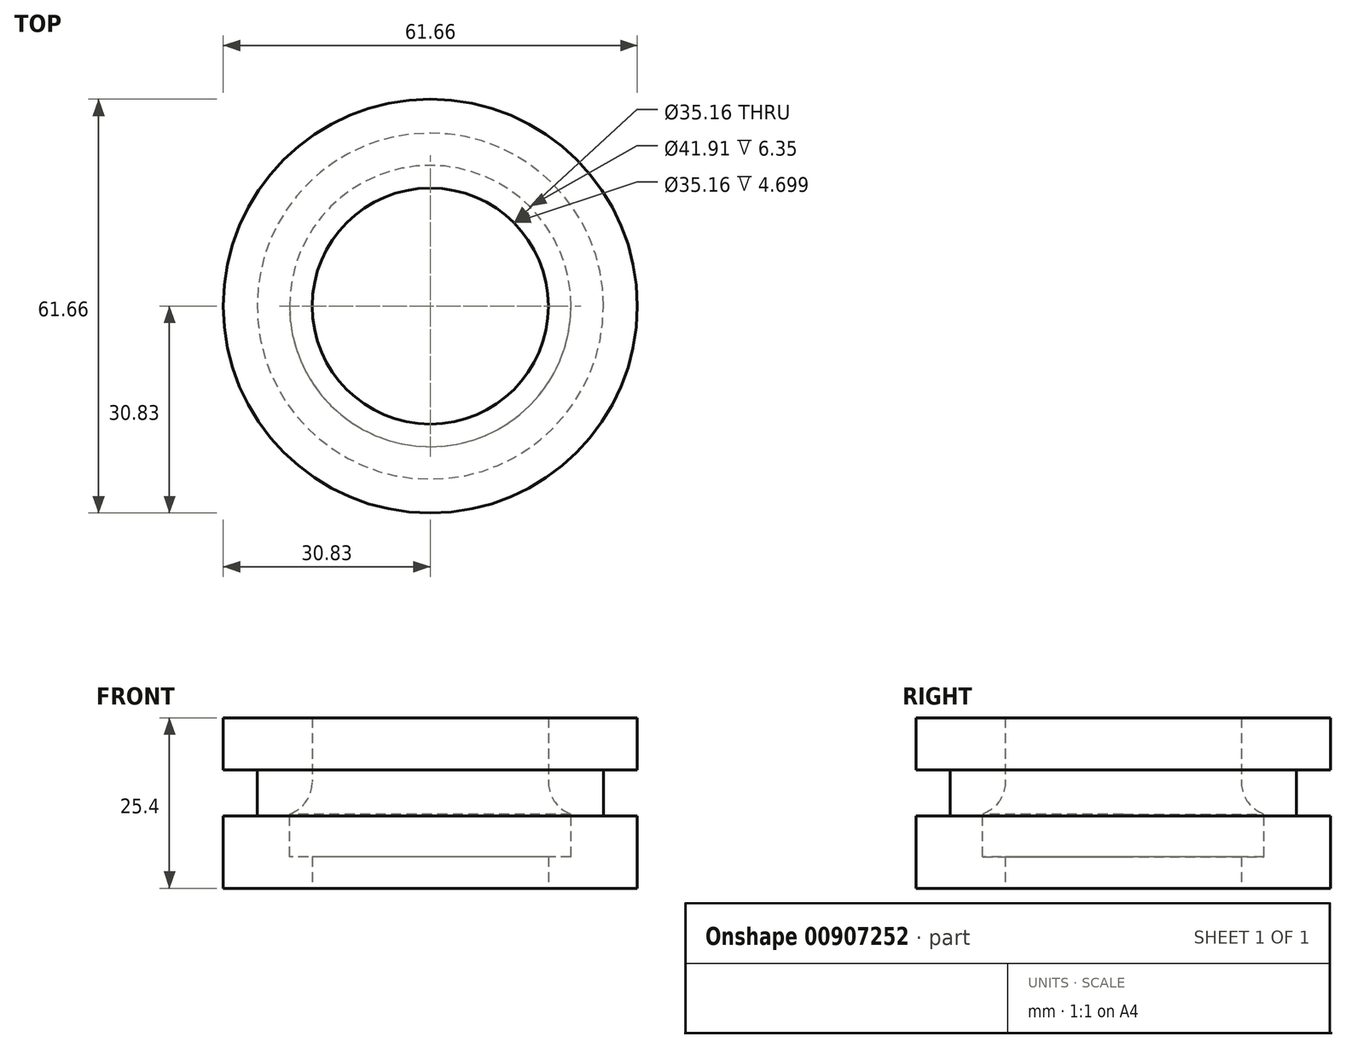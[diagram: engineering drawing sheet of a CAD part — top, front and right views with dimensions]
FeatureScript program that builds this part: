
annotation { "Feature Type Name" : "Feature", "Feature Type Description" : "" }
export const myFeature = defineFeature(function(context is Context, id is Id, definition is map)
    precondition{}
    {
        {
            var Q0;
            Q0=qCreatedBy(makeId("Top.planeOp"),FACE);
            var sketch = newSketch(context, id + "F0", { "sketchPlane" : qUnion([Q0])});
            skCircle(sketch, "E0", {"center": v(0, 0) * mm, "radius": 30.83 * mm});
            skCircle(sketch, "E1", {"center": v(0, 0) * mm, "radius": 17.58 * mm});
            skSolve(sketch);
        }
        {
            var Q0;
            Q0 = qSketchRegion(id + "F0", true);
            extrude(context, id + "F1", {"entities" : qUnion([Q0]), "depth" : 25.4 * mm, "offsetDistance" : 25.4 * mm});
        }
        {
            var Q0;
            Q0=qCreatedBy(makeId("Front.planeOp"),FACE);
            var sketch = newSketch(context, id + "F2", { "sketchPlane" : qUnion([Q0])});
            skLineSegment(sketch, "E2.bottom", {"start": v(25.78, 17.65) * mm, "end": v(31.62, 17.65) * mm});
            skLineSegment(sketch, "E2.top", {"start": v(25.78, 10.8) * mm, "end": v(31.62, 10.8) * mm});
            skLineSegment(sketch, "E2.left", {"start": v(25.78, 17.65) * mm, "end": v(25.78, 10.8) * mm});
            skLineSegment(sketch, "E2.right", {"start": v(31.62, 17.65) * mm, "end": v(31.62, 10.8) * mm});
            skLineSegment(sketch, "E3.bottom", {"start": v(12.83, 11.05) * mm, "end": v(20.96, 11.05) * mm});
            skLineSegment(sketch, "E3.top", {"start": v(12.83, 4.7) * mm, "end": v(20.96, 4.7) * mm});
            skLineSegment(sketch, "E3.left", {"start": v(12.83, 11.05) * mm, "end": v(12.83, 4.7) * mm});
            skLineSegment(sketch, "E3.right", {"start": v(20.96, 11.05) * mm, "end": v(20.96, 4.7) * mm});
            skSolve(sketch);
        }
        {
            var Q0;
            Q0 = qSketchRegion(id + "F2", true);
            var Q1;
            Q1=makeQuery(id+"F1.opExtrude","SWEPT_FACE",FACE,{"disambiguationData":[OSD([sQuery(id+"F0.wireOp",EDGE,"E1")])]});
            revolve(context, id + "F3", {"operationType" : NewBodyOperationType.REMOVE, "surfaceOperationType" : NewSurfaceOperationType.NEW, "entities" : qUnion([Q0]), "axis" : qUnion([Q1]), "revolveType" : RevolveType.FULL, "oppositeDirection" : true});
        }
        {
            var Q0;
            Q0=makeQuery(id+"F3.boolean.opBoolean","INTERSECT",EDGE,{"derivedFrom":[makeQuery(id+"F1.opExtrude","SWEPT_FACE",FACE,{"disambiguationData":[OSD([sQuery(id+"F0.wireOp",EDGE,"E1")])]}),makeQuery(id+"F3.opRevolve","SWEPT_FACE",FACE,{"disambiguationData":[OSD([sQuery(id+"F2.wireOp",EDGE,"E3.bottom")])]})]});
            fillet(context, id + "F4", {"entities" : qUnion([Q0]), "radius" : 5.08 * mm, "tangentPropagation" : true, "allowEdgeOverflow" : false});
        }
    });
